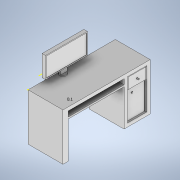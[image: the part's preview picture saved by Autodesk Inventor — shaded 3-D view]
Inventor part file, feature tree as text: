
AUTODESK INVENTOR PART (.ipt)
format: ipt  version: 2022 (Build 260153000, 153)  size: 302,592 bytes
history: native  units: mm
features: sketch x16, extrude x14, fillet x5, plane x2, shell x1, loft x1
ambient origin geometry x8: Origin, YZ Plane, XZ Plane, XY Plane, X Axis, Y Axis, Z Axis, Center Point
bodies: Solid1 (feature_tree)
feature tree (39):
  extrude  "Extrusion1"  Depth=10.0mm
  sketch  "Sketch2"  dims[d2=1.0mm d3=0.0mm d4=1.5mm]
  extrude  "Extrusion2"  Depth=1.5mm
  extrude  "Extrusion3"  Depth=7.5mm
  extrude  "Extrusion5"  Depth=25.0mm
  fillet  "Fillet1"  Radius=1.0mm
  shell  "Shell1"  Thickness=2.0mm
  extrude  "Extrusion6"  Depth=2.0mm
  extrude  "Extrusion7"  TaperAngle=0.0deg  [1 undecoded]
  fillet  "Fillet2"  Radius=7.0mm
  extrude  "Extrusion8"  Depth=0.1mm
  fillet  "Fillet3"  Radius=1.0mm
  sketch  "Sketch7"  dims[d20=0.0mm d21=0.0mm d22=0.1mm d23=1.0mm]
  plane  "Work Plane1"
  loft  "Loft1"
  fillet  "Fillet4"  [1 undecoded]
  fillet  "Fillet5"  Radius=8.0mm
  sketch  "Sketch9"  dims[d28=8.5mm d29=0.0mm d30=0.5mm]
  plane  "Work Plane2"
  sketch  "Sketch10"  dims[d31=1.5mm d32=1.5mm]
  extrude  "Extrusion9"  Depth=0.5mm
  extrude  "Extrusion10"  Depth=1.5mm
  extrude  "Extrusion11"  Depth=0.05mm
  extrude  "Extrusion12"  Depth=0.05mm
  extrude  "Extrusion13"  Depth=3.4mm
  extrude  "Extrusion14"  Depth=0.15mm
  extrude  "Extrusion15"  Depth=1.55mm
  sketch  "Sketch16"  dims[d45=2.55mm d46=0.5mm d47=0.5mm d48=0.0mm d49=90.0deg d50=0.0mm d51=90.0deg d52=0.075mm d53=0.075mm d54=-1.0mm d55=12.0mm d56=6.0mm d57=2.0mm d58=3.0mm d59=0.25mm d60=1.0mm d61=0.0mm d62=0.9mm d63=0.0mm d64=3.5mm d65=0.0mm d66=1.75mm d67=0.75mm d68=1.75mm d69=0.75mm d70=10.0mm d71=0.0mm d72=10.0mm d73=0.0mm d74=2.5mm d75=2.5mm d76=0.5mm d77=1.0mm d78=0.0mm d79=16.0mm d80=0.5mm d81=1.0mm d82=0.0mm d83=0.1mm d84=0.872665mm d85=0.5mm d86=0.872665mm]
  sketch  "Sketch1"  dims[d0=25.0mm d1=10.0mm]
  sketch  "Sketch3"  dims[d5=10.0mm d6=7.5mm]
  sketch  "Sketch4"  dims[d7=10.0mm d8=25.0mm d9=1.0mm d10=2.0mm d11=0.0mm]
  sketch  "Sketch5"  dims[d12=12.5mm d13=0.0mm d16=2.0mm]
  sketch  "Sketch6"  dims[d17=0.5mm d18=0.0mm d19=7.0mm]
  sketch  "Sketch8"  dims[d24=5.0mm d25=0.25mm d26=0.0mm d27=8.0mm]
  sketch  "Sketch11"  dims[d33=0.1mm d34=0.0mm d35=0.05mm]
  sketch  "Sketch12"  dims[d36=5.4mm d37=0.05mm]
  sketch  "Sketch13"  dims[d38=0.05mm d39=3.4mm]
  sketch  "Sketch14"  dims[d40=9.0mm d41=0.0mm d42=0.15mm]
  sketch  "Sketch15"  dims[d43=0.3mm d44=1.55mm]
note: 2 required parameter values undecoded (feature->parameter linkage not recoverable at this tier; creation-order binding heuristic only, values carry confidence <= 0.55)
